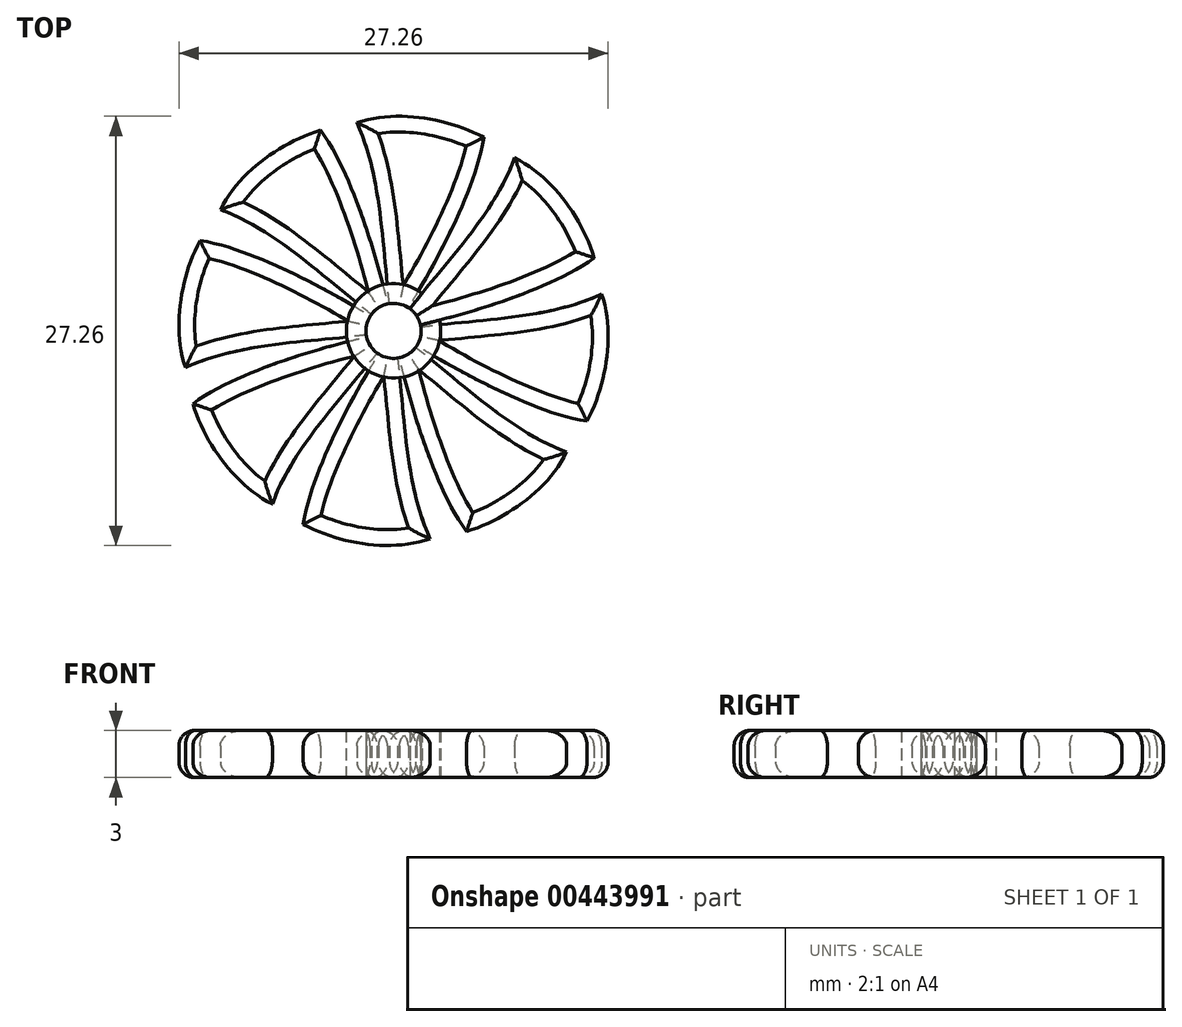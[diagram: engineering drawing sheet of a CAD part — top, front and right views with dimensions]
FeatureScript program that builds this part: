
annotation { "Feature Type Name" : "Feature", "Feature Type Description" : "" }
export const myFeature = defineFeature(function(context is Context, id is Id, definition is map)
    precondition{}
    {
        {
            var Q0;
            Q0=qCreatedBy(makeId("Top.planeOp"),FACE);
            var sketch = newSketch(context, id + "F0", { "sketchPlane" : qUnion([Q0])});
            skCircle(sketch, "E0", {"center": v(0, 0) * mm, "radius": 14 * mm});
            skLineSegment(sketch, "E1", {"start": v(0, 0) * mm, "end": v(0, 14) * mm, "construction": true});
            skLineSegment(sketch, "E2", {"start": v(0, 0) * mm, "end": v(9.9, 9.9) * mm, "construction": true});
            skLineSegment(sketch, "E3.MirrorCS", {"start": v(0, 0) * mm, "end": v(14, 0) * mm, "construction": true});
            skLineSegment(sketch, "E4.MirrorCS", {"start": v(0, 0) * mm, "end": v(9.9, -9.9) * mm});
            skLineSegment(sketch, "E5.MirrorCS", {"start": v(0, 0) * mm, "end": v(0, -14) * mm, "construction": true});
            skLineSegment(sketch, "E6.MirrorCS", {"start": v(0, 0) * mm, "end": v(-9.9, -9.9) * mm, "construction": true});
            skLineSegment(sketch, "E7.MirrorCS", {"start": v(0, 0) * mm, "end": v(-14, 0) * mm, "construction": true});
            skCircle(sketch, "E8", {"center": v(0, 0) * mm, "radius": 1.75 * mm});
            skLineSegment(sketch, "E9", {"start": v(0, 0) * mm, "end": v(-9.9, 9.9) * mm, "construction": true});
            skLineSegment(sketch, "E10", {"start": v(0, 0) * mm, "end": v(8.03, 11.47) * mm, "construction": true});
            skLineSegment(sketch, "E11", {"start": v(0, 0) * mm, "end": v(13.16, 4.79) * mm, "construction": true});
            skFitSpline(sketch, "E12", {"points": [v(7.7, 11) * mm, v(12.75, 4.64) * mm], "startDerivative": vector(6.6, -3.29) * mm, "endDerivative": vector(2.7, -8.46) * mm});
            skFitSpline(sketch, "E13", {"points": [v(0, 0) * mm, v(7.7, 11) * mm], "startDerivative": vector(7.7, 11) * mm, "endDerivative": vector(4.5, 12.16) * mm});
            skFitSpline(sketch, "E14", {"points": [v(0, 0) * mm, v(12.75, 4.64) * mm], "startDerivative": vector(14.05, 2.9) * mm, "endDerivative": vector(7.7, 5.76) * mm});
            skCircle(sketch, "E15", {"center": v(0, 0) * mm, "radius": 3 * mm});
            skSolve(sketch);
        }
        {
            var Q0;
            {var subQ0=sQuery(id+"F0.wireOp",EDGE,"E12");Q0=makeQuery(id+"F0.imprint","IMPRINT",FACE,{"disambiguationData":[TD([[makeQuery(id+"F0.imprint","IMPRINT",EDGE,{"derivedFrom":subQ0}),-1.0]])]});}
            var Q1;
            {var subQ0=sQuery(id+"F0.wireOp",EDGE,"E13");var subQ1=sQuery(id+"F0.wireOp",EDGE,"E8");var subQ2=makeQuery(id+"F0.imprint","INTERSECT",VERTEX,{"derivedFrom":[subQ1,subQ0]});Q1=makeQuery(id+"F0.imprint","IMPRINT",FACE,{"disambiguationData":[TD([[makeQuery(id+"F0.imprint","IMPRINT",EDGE,{"disambiguationData":[TD([[subQ2,1.0]])],"derivedFrom":subQ1}),-1.0]])]});}
            extrude(context, id + "F1", {"entities" : qUnion([Q0, Q1]), "depth" : 3 * mm});
        }
        {
            var Q0;
            Q0=makeQuery(id+"F1.opExtrude","SWEPT_BODY",BODY,{"disambiguationData":[OSD([sQuery(id+"F0.wireOp",EDGE,"E8"),sQuery(id+"F0.wireOp",EDGE,"E12"),sQuery(id+"F0.wireOp",EDGE,"E13"),sQuery(id+"F0.wireOp",EDGE,"E14")])]});
            var Q1;
            Q1=sQuery(id+"F0.wireOp",EDGE,"E8");
            circularPattern(context, id + "F2", {"entities" : qUnion([Q0]), "axis" : qUnion([Q1]), "angle" : 360 * degree, "instanceCount" : 8, "equalSpace" : true});
        }
        {
            var Q0;
            {var subQ0=sQuery(id+"F0.wireOp",EDGE,"E15");var subQ1=sQuery(id+"F0.wireOp",EDGE,"E4.MirrorCS");var subQ2=makeQuery(id+"F0.imprint","INTERSECT",VERTEX,{"derivedFrom":[subQ1,subQ0]});Q0=makeQuery(id+"F0.imprint","IMPRINT",FACE,{"disambiguationData":[TD([[makeQuery(id+"F0.imprint","IMPRINT",EDGE,{"disambiguationData":[TD([[subQ2,1.0]])],"derivedFrom":subQ1}),1.0]])]});}
            var Q1;
            {var subQ0=sQuery(id+"F0.wireOp",EDGE,"E15");var subQ1=sQuery(id+"F0.wireOp",EDGE,"E4.MirrorCS");var subQ2=makeQuery(id+"F0.imprint","INTERSECT",VERTEX,{"derivedFrom":[subQ1,subQ0]});Q1=makeQuery(id+"F0.imprint","IMPRINT",FACE,{"disambiguationData":[TD([[makeQuery(id+"F0.imprint","IMPRINT",EDGE,{"disambiguationData":[TD([[subQ2,1.0]])],"derivedFrom":subQ1}),-1.0]])]});}
            extrude(context, id + "F3", {"entities" : qUnion([Q0, Q1]), "depth" : 3 * mm});
        }
        {
            var Q0;
            Q0=makeQuery(id+"F2.opPattern","COPY",EDGE,{"derivedFrom":makeQuery(id+"F1.opExtrude","CAP_EDGE",EDGE,{"disambiguationData":[OSD([sQuery(id+"F0.wireOp",EDGE,"E12")])],"isStart":false}),"instanceName":"3"});
            var Q1;
            Q1=makeQuery(id+"F2.opPattern","COPY",EDGE,{"derivedFrom":makeQuery(id+"F1.opExtrude","CAP_EDGE",EDGE,{"disambiguationData":[OSD([sQuery(id+"F0.wireOp",EDGE,"E13")])],"isStart":false}),"instanceName":"3"});
            var Q2;
            Q2=makeQuery(id+"F2.opPattern","COPY",EDGE,{"derivedFrom":makeQuery(id+"F1.opExtrude","CAP_EDGE",EDGE,{"disambiguationData":[OSD([sQuery(id+"F0.wireOp",EDGE,"E14")])],"isStart":false}),"instanceName":"3"});
            var Q3;
            Q3=makeQuery(id+"F2.opPattern","COPY",EDGE,{"derivedFrom":makeQuery(id+"F1.opExtrude","CAP_EDGE",EDGE,{"disambiguationData":[OSD([sQuery(id+"F0.wireOp",EDGE,"E13")])],"isStart":false}),"instanceName":"2"});
            var Q4;
            Q4=makeQuery(id+"F2.opPattern","COPY",EDGE,{"derivedFrom":makeQuery(id+"F1.opExtrude","CAP_EDGE",EDGE,{"disambiguationData":[OSD([sQuery(id+"F0.wireOp",EDGE,"E12")])],"isStart":false}),"instanceName":"2"});
            var Q5;
            Q5=makeQuery(id+"F2.opPattern","COPY",EDGE,{"derivedFrom":makeQuery(id+"F1.opExtrude","CAP_EDGE",EDGE,{"disambiguationData":[OSD([sQuery(id+"F0.wireOp",EDGE,"E14")])],"isStart":false}),"instanceName":"2"});
            var Q6;
            Q6=makeQuery(id+"F2.opPattern","COPY",EDGE,{"derivedFrom":makeQuery(id+"F1.opExtrude","CAP_EDGE",EDGE,{"disambiguationData":[OSD([sQuery(id+"F0.wireOp",EDGE,"E13")])],"isStart":false}),"instanceName":"1"});
            var Q7;
            Q7=makeQuery(id+"F2.opPattern","COPY",EDGE,{"derivedFrom":makeQuery(id+"F1.opExtrude","CAP_EDGE",EDGE,{"disambiguationData":[OSD([sQuery(id+"F0.wireOp",EDGE,"E12")])],"isStart":false}),"instanceName":"1"});
            var Q8;
            Q8=makeQuery(id+"F2.opPattern","COPY",EDGE,{"derivedFrom":makeQuery(id+"F1.opExtrude","CAP_EDGE",EDGE,{"disambiguationData":[OSD([sQuery(id+"F0.wireOp",EDGE,"E14")])],"isStart":false}),"instanceName":"1"});
            var Q9;
            Q9=makeQuery(id+"F1.opExtrude","CAP_EDGE",EDGE,{"disambiguationData":[OSD([sQuery(id+"F0.wireOp",EDGE,"E13")])],"isStart":false});
            var Q10;
            Q10=makeQuery(id+"F1.opExtrude","CAP_EDGE",EDGE,{"disambiguationData":[OSD([sQuery(id+"F0.wireOp",EDGE,"E12")])],"isStart":false});
            var Q11;
            Q11=makeQuery(id+"F1.opExtrude","CAP_EDGE",EDGE,{"disambiguationData":[OSD([sQuery(id+"F0.wireOp",EDGE,"E14")])],"isStart":false});
            var Q12;
            Q12=makeQuery(id+"F2.opPattern","COPY",EDGE,{"derivedFrom":makeQuery(id+"F1.opExtrude","CAP_EDGE",EDGE,{"disambiguationData":[OSD([sQuery(id+"F0.wireOp",EDGE,"E13")])],"isStart":false}),"instanceName":"7"});
            var Q13;
            Q13=makeQuery(id+"F2.opPattern","COPY",EDGE,{"derivedFrom":makeQuery(id+"F1.opExtrude","CAP_EDGE",EDGE,{"disambiguationData":[OSD([sQuery(id+"F0.wireOp",EDGE,"E12")])],"isStart":false}),"instanceName":"7"});
            var Q14;
            Q14=makeQuery(id+"F2.opPattern","COPY",EDGE,{"derivedFrom":makeQuery(id+"F1.opExtrude","CAP_EDGE",EDGE,{"disambiguationData":[OSD([sQuery(id+"F0.wireOp",EDGE,"E14")])],"isStart":false}),"instanceName":"7"});
            var Q15;
            Q15=makeQuery(id+"F2.opPattern","COPY",EDGE,{"derivedFrom":makeQuery(id+"F1.opExtrude","CAP_EDGE",EDGE,{"disambiguationData":[OSD([sQuery(id+"F0.wireOp",EDGE,"E13")])],"isStart":false}),"instanceName":"6"});
            var Q16;
            Q16=makeQuery(id+"F2.opPattern","COPY",EDGE,{"derivedFrom":makeQuery(id+"F1.opExtrude","CAP_EDGE",EDGE,{"disambiguationData":[OSD([sQuery(id+"F0.wireOp",EDGE,"E14")])],"isStart":false}),"instanceName":"6"});
            var Q17;
            Q17=makeQuery(id+"F2.opPattern","COPY",EDGE,{"derivedFrom":makeQuery(id+"F1.opExtrude","CAP_EDGE",EDGE,{"disambiguationData":[OSD([sQuery(id+"F0.wireOp",EDGE,"E13")])],"isStart":false}),"instanceName":"5"});
            var Q18;
            Q18=makeQuery(id+"F2.opPattern","COPY",EDGE,{"derivedFrom":makeQuery(id+"F1.opExtrude","CAP_EDGE",EDGE,{"disambiguationData":[OSD([sQuery(id+"F0.wireOp",EDGE,"E14")])],"isStart":false}),"instanceName":"5"});
            var Q19;
            Q19=makeQuery(id+"F2.opPattern","COPY",EDGE,{"derivedFrom":makeQuery(id+"F1.opExtrude","CAP_EDGE",EDGE,{"disambiguationData":[OSD([sQuery(id+"F0.wireOp",EDGE,"E13")])],"isStart":false}),"instanceName":"4"});
            var Q20;
            Q20=makeQuery(id+"F2.opPattern","COPY",EDGE,{"derivedFrom":makeQuery(id+"F1.opExtrude","CAP_EDGE",EDGE,{"disambiguationData":[OSD([sQuery(id+"F0.wireOp",EDGE,"E14")])],"isStart":false}),"instanceName":"4"});
            var Q21;
            Q21=makeQuery(id+"F2.opPattern","COPY",EDGE,{"derivedFrom":makeQuery(id+"F1.opExtrude","CAP_EDGE",EDGE,{"disambiguationData":[OSD([sQuery(id+"F0.wireOp",EDGE,"E12")])],"isStart":false}),"instanceName":"4"});
            var Q22;
            Q22=makeQuery(id+"F2.opPattern","COPY",EDGE,{"derivedFrom":makeQuery(id+"F1.opExtrude","CAP_EDGE",EDGE,{"disambiguationData":[OSD([sQuery(id+"F0.wireOp",EDGE,"E12")])],"isStart":false}),"instanceName":"5"});
            var Q23;
            Q23=makeQuery(id+"F2.opPattern","COPY",EDGE,{"derivedFrom":makeQuery(id+"F1.opExtrude","CAP_EDGE",EDGE,{"disambiguationData":[OSD([sQuery(id+"F0.wireOp",EDGE,"E12")])],"isStart":false}),"instanceName":"6"});
            fillet(context, id + "F4", {"entities" : qUnion([Q0, Q1, Q2, Q3, Q4, Q5, Q6, Q7, Q8, Q9, Q10, Q11, Q12, Q13, Q14, Q15, Q16, Q17, Q18, Q19, Q20, Q21, Q22, Q23]), "radius" : 1 * mm, "tangentPropagation" : true, "allowEdgeOverflow" : false});
        }
        {
            var Q0;
            Q0=makeQuery(id+"F1.opExtrude","CAP_EDGE",EDGE,{"disambiguationData":[OSD([sQuery(id+"F0.wireOp",EDGE,"E13")])],"isStart":true});
            var Q1;
            Q1=makeQuery(id+"F1.opExtrude","CAP_EDGE",EDGE,{"disambiguationData":[OSD([sQuery(id+"F0.wireOp",EDGE,"E12")])],"isStart":true});
            var Q2;
            Q2=makeQuery(id+"F1.opExtrude","CAP_EDGE",EDGE,{"disambiguationData":[OSD([sQuery(id+"F0.wireOp",EDGE,"E14")])],"isStart":true});
            var Q3;
            Q3=makeQuery(id+"F2.opPattern","COPY",EDGE,{"derivedFrom":makeQuery(id+"F1.opExtrude","CAP_EDGE",EDGE,{"disambiguationData":[OSD([sQuery(id+"F0.wireOp",EDGE,"E14")])],"isStart":true}),"instanceName":"1"});
            var Q4;
            Q4=makeQuery(id+"F2.opPattern","COPY",EDGE,{"derivedFrom":makeQuery(id+"F1.opExtrude","CAP_EDGE",EDGE,{"disambiguationData":[OSD([sQuery(id+"F0.wireOp",EDGE,"E12")])],"isStart":true}),"instanceName":"1"});
            var Q5;
            Q5=makeQuery(id+"F2.opPattern","COPY",EDGE,{"derivedFrom":makeQuery(id+"F1.opExtrude","CAP_EDGE",EDGE,{"disambiguationData":[OSD([sQuery(id+"F0.wireOp",EDGE,"E13")])],"isStart":true}),"instanceName":"1"});
            var Q6;
            Q6=makeQuery(id+"F2.opPattern","COPY",EDGE,{"derivedFrom":makeQuery(id+"F1.opExtrude","CAP_EDGE",EDGE,{"disambiguationData":[OSD([sQuery(id+"F0.wireOp",EDGE,"E14")])],"isStart":true}),"instanceName":"2"});
            var Q7;
            Q7=makeQuery(id+"F2.opPattern","COPY",EDGE,{"derivedFrom":makeQuery(id+"F1.opExtrude","CAP_EDGE",EDGE,{"disambiguationData":[OSD([sQuery(id+"F0.wireOp",EDGE,"E12")])],"isStart":true}),"instanceName":"2"});
            var Q8;
            Q8=makeQuery(id+"F2.opPattern","COPY",EDGE,{"derivedFrom":makeQuery(id+"F1.opExtrude","CAP_EDGE",EDGE,{"disambiguationData":[OSD([sQuery(id+"F0.wireOp",EDGE,"E13")])],"isStart":true}),"instanceName":"2"});
            var Q9;
            Q9=makeQuery(id+"F2.opPattern","COPY",EDGE,{"derivedFrom":makeQuery(id+"F1.opExtrude","CAP_EDGE",EDGE,{"disambiguationData":[OSD([sQuery(id+"F0.wireOp",EDGE,"E14")])],"isStart":true}),"instanceName":"3"});
            var Q10;
            Q10=makeQuery(id+"F2.opPattern","COPY",EDGE,{"derivedFrom":makeQuery(id+"F1.opExtrude","CAP_EDGE",EDGE,{"disambiguationData":[OSD([sQuery(id+"F0.wireOp",EDGE,"E12")])],"isStart":true}),"instanceName":"3"});
            var Q11;
            Q11=makeQuery(id+"F2.opPattern","COPY",EDGE,{"derivedFrom":makeQuery(id+"F1.opExtrude","CAP_EDGE",EDGE,{"disambiguationData":[OSD([sQuery(id+"F0.wireOp",EDGE,"E13")])],"isStart":true}),"instanceName":"3"});
            var Q12;
            Q12=makeQuery(id+"F2.opPattern","COPY",EDGE,{"derivedFrom":makeQuery(id+"F1.opExtrude","CAP_EDGE",EDGE,{"disambiguationData":[OSD([sQuery(id+"F0.wireOp",EDGE,"E14")])],"isStart":true}),"instanceName":"4"});
            var Q13;
            Q13=makeQuery(id+"F2.opPattern","COPY",EDGE,{"derivedFrom":makeQuery(id+"F1.opExtrude","CAP_EDGE",EDGE,{"disambiguationData":[OSD([sQuery(id+"F0.wireOp",EDGE,"E12")])],"isStart":true}),"instanceName":"4"});
            var Q14;
            Q14=makeQuery(id+"F2.opPattern","COPY",EDGE,{"derivedFrom":makeQuery(id+"F1.opExtrude","CAP_EDGE",EDGE,{"disambiguationData":[OSD([sQuery(id+"F0.wireOp",EDGE,"E13")])],"isStart":true}),"instanceName":"4"});
            var Q15;
            Q15=makeQuery(id+"F2.opPattern","COPY",EDGE,{"derivedFrom":makeQuery(id+"F1.opExtrude","CAP_EDGE",EDGE,{"disambiguationData":[OSD([sQuery(id+"F0.wireOp",EDGE,"E14")])],"isStart":true}),"instanceName":"5"});
            var Q16;
            Q16=makeQuery(id+"F2.opPattern","COPY",EDGE,{"derivedFrom":makeQuery(id+"F1.opExtrude","CAP_EDGE",EDGE,{"disambiguationData":[OSD([sQuery(id+"F0.wireOp",EDGE,"E13")])],"isStart":true}),"instanceName":"5"});
            var Q17;
            Q17=makeQuery(id+"F2.opPattern","COPY",EDGE,{"derivedFrom":makeQuery(id+"F1.opExtrude","CAP_EDGE",EDGE,{"disambiguationData":[OSD([sQuery(id+"F0.wireOp",EDGE,"E13")])],"isStart":true}),"instanceName":"7"});
            var Q18;
            Q18=makeQuery(id+"F2.opPattern","COPY",EDGE,{"derivedFrom":makeQuery(id+"F1.opExtrude","CAP_EDGE",EDGE,{"disambiguationData":[OSD([sQuery(id+"F0.wireOp",EDGE,"E12")])],"isStart":true}),"instanceName":"7"});
            var Q19;
            Q19=makeQuery(id+"F2.opPattern","COPY",EDGE,{"derivedFrom":makeQuery(id+"F1.opExtrude","CAP_EDGE",EDGE,{"disambiguationData":[OSD([sQuery(id+"F0.wireOp",EDGE,"E14")])],"isStart":true}),"instanceName":"7"});
            var Q20;
            Q20=makeQuery(id+"F2.opPattern","COPY",EDGE,{"derivedFrom":makeQuery(id+"F1.opExtrude","CAP_EDGE",EDGE,{"disambiguationData":[OSD([sQuery(id+"F0.wireOp",EDGE,"E13")])],"isStart":true}),"instanceName":"6"});
            var Q21;
            Q21=makeQuery(id+"F2.opPattern","COPY",EDGE,{"derivedFrom":makeQuery(id+"F1.opExtrude","CAP_EDGE",EDGE,{"disambiguationData":[OSD([sQuery(id+"F0.wireOp",EDGE,"E14")])],"isStart":true}),"instanceName":"6"});
            var Q22;
            Q22=makeQuery(id+"F2.opPattern","COPY",EDGE,{"derivedFrom":makeQuery(id+"F1.opExtrude","CAP_EDGE",EDGE,{"disambiguationData":[OSD([sQuery(id+"F0.wireOp",EDGE,"E12")])],"isStart":true}),"instanceName":"5"});
            var Q23;
            Q23=makeQuery(id+"F2.opPattern","COPY",EDGE,{"derivedFrom":makeQuery(id+"F1.opExtrude","CAP_EDGE",EDGE,{"disambiguationData":[OSD([sQuery(id+"F0.wireOp",EDGE,"E12")])],"isStart":true}),"instanceName":"6"});
            fillet(context, id + "F5", {"entities" : qUnion([Q0, Q1, Q2, Q3, Q4, Q5, Q6, Q7, Q8, Q9, Q10, Q11, Q12, Q13, Q14, Q15, Q16, Q17, Q18, Q19, Q20, Q21, Q22, Q23]), "radius" : 1 * mm, "tangentPropagation" : true, "allowEdgeOverflow" : false});
        }
    });
